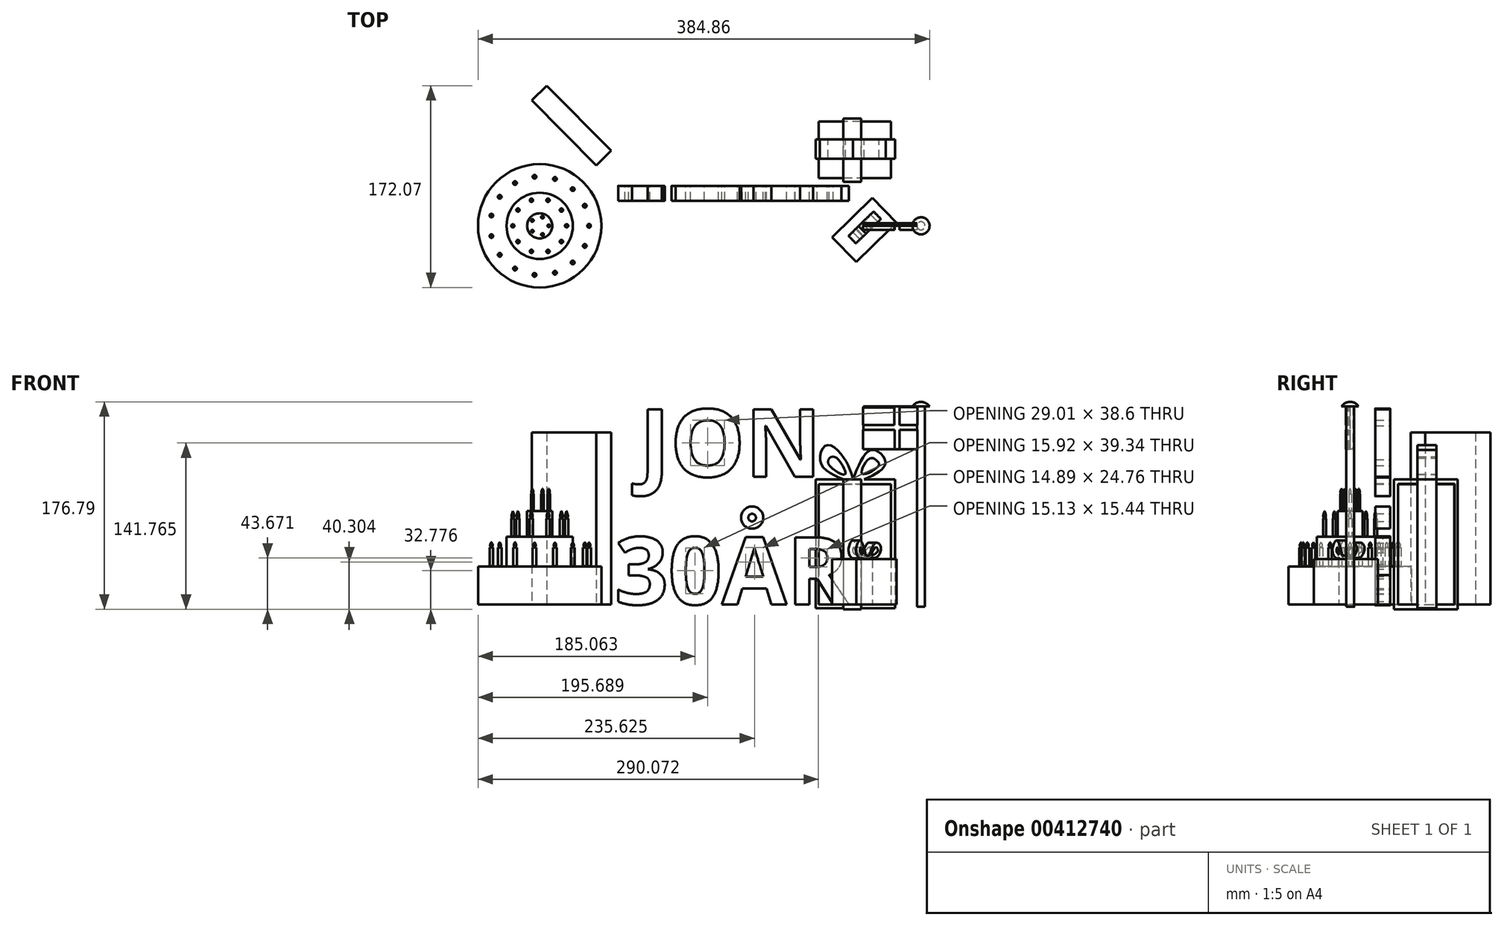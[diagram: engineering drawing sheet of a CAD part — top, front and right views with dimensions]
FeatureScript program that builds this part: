
annotation { "Feature Type Name" : "Feature", "Feature Type Description" : "" }
export const myFeature = defineFeature(function(context is Context, id is Id, definition is map)
    precondition{}
    {
        {
            var Q0;
            Q0=qCreatedBy(makeId("Front.planeOp"),FACE);
            var sketch = newSketch(context, id + "F0", { "sketchPlane" : qUnion([Q0])});
            skText(sketch, "E0", { "text": " JON\n30AR", "fontName": "OpenSans-Bold.ttf"});
            skCircle(sketch, "E1", {"center": v(45.9, -32.52) * mm, "radius": 9.45 * mm});
            skCircle(sketch, "E2", {"center": v(45.9, -32.52) * mm, "radius": 3.24 * mm});
            const initialGuessF0  = {"E0": [-0.07126, 0.00244, 1, 0, 0.05767]};
            skSetInitialGuess(sketch, initialGuessF0);
            skSolve(sketch);
        }
        {
            var Q0;
            Q0 = qSketchRegion(id + "F0", true);
            extrude(context, id + "F1", {"entities" : qUnion([Q0]), "depth" : 12.7 * mm});
        }
        {
            var Q0;
            Q0=qCreatedBy(makeId("Front.planeOp"),FACE);
            cPlane(context, id + "F2", {"entities" : qUnion([Q0]), "cplaneType" : CPlaneType.OFFSET, "offset" : 34.04 * mm, "width" : 152.4 * mm, "height" : 152.4 * mm});
        }
        {
            var Q0;
            Q0=makeQuery(id+"F1.opExtrude","SWEPT_FACE",FACE,{"disambiguationData":[OSD([sQuery(id+"F0.wireOp",EDGE,"E0.sketch_text.stroke-101")])]});
            var sketch = newSketch(context, id + "F3", { "sketchPlane" : qUnion([Q0])});
            skLineSegment(sketch, "E3", {"start": v(148.36, 10.23) * mm, "end": v(114.05, 43.78) * mm});
            skLineSegment(sketch, "E4", {"start": v(114.05, 43.78) * mm, "end": v(134.64, 64.84) * mm});
            skLineSegment(sketch, "E5", {"start": v(134.64, 64.84) * mm, "end": v(168.96, 31.3) * mm});
            skLineSegment(sketch, "E6", {"start": v(148.36, 10.23) * mm, "end": v(168.96, 31.3) * mm});
            skSolve(sketch);
        }
        {
            var Q0;
            Q0 = qSketchRegion(id + "F3", true);
            extrude(context, id + "F4", {"entities" : qUnion([Q0]), "oppositeDirection" : true, "depth" : 38.6 * mm});
        }
        {
            var Q0;
            Q0=makeQuery(id+"F4.opExtrude","SWEPT_FACE",FACE,{"disambiguationData":[OSD([sQuery(id+"F3.wireOp",EDGE,"E5")])]});
            cPlane(context, id + "F5", {"entities" : qUnion([Q0]), "cplaneType" : CPlaneType.OFFSET, "offset" : 16 * mm, "oppositeDirection" : true, "width" : 152.4 * mm, "height" : 152.4 * mm});
        }
        {
            var Q0;
            Q0=qCreatedBy(id+"F5.planeOp",FACE);
            var sketch = newSketch(context, id + "F6", { "sketchPlane" : qUnion([Q0])});
            skLineSegment(sketch, "E7", {"start": v(79.86, -67.82) * mm, "end": v(79.86, -66.38) * mm});
            skLineSegment(sketch, "E8", {"start": v(77.86, -64.93) * mm, "end": v(73.66, -64.93) * mm});
            skLineSegment(sketch, "E9", {"start": v(70.9, -67.21) * mm, "end": v(70.9, -68.06) * mm});
            skLineSegment(sketch, "E10", {"start": v(70.9, -68.06) * mm, "end": v(79.86, -67.82) * mm});
            skFitSpline(sketch, "E11", {"points": [v(77.86, -64.93) * mm, v(85.68, -53.9) * mm, v(91.43, -57.45) * mm, v(87.3, -66.01) * mm, v(79.86, -66.38) * mm], "startDerivative": vector(22.46, 50.64) * mm, "endDerivative": vector(-34.08, 6.92) * mm});
            skFitSpline(sketch, "E12", {"points": [v(80.8, -64.15) * mm, v(85.47, -57.91) * mm, v(87.84, -59.57) * mm, v(86.68, -62.36) * mm, v(80.8, -64.15) * mm]});
            skFitSpline(sketch, "E13", {"points": [v(73.66, -64.93) * mm, v(66.7, -52) * mm, v(61.8, -59.78) * mm, v(65.46, -66.74) * mm, v(70.9, -67.21) * mm], "startDerivative": vector(-19.87, 61.15) * mm, "endDerivative": vector(28.8, 3.24) * mm});
            skFitSpline(sketch, "E14", {"points": [v(70, -63.21) * mm, v(67.74, -58.1) * mm, v(67.06, -62.13) * mm, v(70, -63.21) * mm]});
            skPoint(sketch, "E15.orphan", {"position": v(79.86, -64.93) * mm});
            skSolve(sketch);
        }
        {
            var Q0;
            Q0 = qSketchRegion(id + "F6", true);
            extrude(context, id + "F7", {"entities" : qUnion([Q0]), "operationType" : NewBodyOperationType.ADD, "endBound" : BoundingType.SYMMETRIC, "depth" : 8.97 * mm});
        }
        {
            var Q0;
            Q0=makeQuery(id+"F1.opExtrude","SWEPT_FACE",FACE,{"disambiguationData":[OSD([sQuery(id+"F0.wireOp",EDGE,"E0.sketch_text.stroke-101")])]});
            var sketch = newSketch(context, id + "F8", { "sketchPlane" : qUnion([Q0])});
            skLineSegment(sketch, "E16.bottom", {"start": v(164.28, -6.74) * mm, "end": v(102.72, -6.74) * mm});
            skLineSegment(sketch, "E16.top", {"start": v(164.28, -54.83) * mm, "end": v(102.72, -54.83) * mm});
            skLineSegment(sketch, "E16.left", {"start": v(164.28, -6.74) * mm, "end": v(164.28, -54.83) * mm});
            skLineSegment(sketch, "E16.right", {"start": v(102.72, -6.74) * mm, "end": v(102.72, -54.83) * mm});
            skSolve(sketch);
        }
        {
            var Q0;
            Q0=makeQuery(id+"F8.imprint","IMPRINT",FACE,{"disambiguationData":[TD([[makeQuery(id+"F8.imprint","IMPRINT",EDGE,{"derivedFrom":sQuery(id+"F8.wireOp",EDGE,"E16.bottom")}),1.0]])]});
            extrude(context, id + "F9", {"entities" : qUnion([Q0]), "oppositeDirection" : true, "depth" : 102.36 * mm});
        }
        {
            var Q0;
            Q0=makeQuery(id+"F9.opExtrude","SWEPT_FACE",FACE,{"disambiguationData":[OSD([sQuery(id+"F8.wireOp",EDGE,"E16.left")])]});
            cPlane(context, id + "F10", {"entities" : qUnion([Q0]), "cplaneType" : CPlaneType.OFFSET, "offset" : 33.02 * mm, "oppositeDirection" : true, "width" : 152.4 * mm, "height" : 152.4 * mm});
        }
        {
            var Q0;
            Q0=qCreatedBy(id+"F10.planeOp",FACE);
            var sketch = newSketch(context, id + "F11", { "sketchPlane" : qUnion([Q0])});
            skLineSegment(sketch, "E17.bottom", {"start": v(6.87, -3.88) * mm, "end": v(54.94, -3.88) * mm});
            skLineSegment(sketch, "E17.top", {"start": v(6.87, -106.27) * mm, "end": v(54.94, -106.27) * mm});
            skLineSegment(sketch, "E17.left", {"start": v(6.87, -3.88) * mm, "end": v(6.87, -106.27) * mm});
            skLineSegment(sketch, "E17.right", {"start": v(54.94, -3.88) * mm, "end": v(54.94, -106.27) * mm});
            skLineSegment(sketch, "E18.bottom", {"start": v(3.43, 0) * mm, "end": v(57.44, 0) * mm});
            skLineSegment(sketch, "E18.top", {"start": v(3.43, -110.64) * mm, "end": v(57.44, -110.64) * mm});
            skLineSegment(sketch, "E18.left", {"start": v(3.43, 0) * mm, "end": v(3.43, -110.64) * mm});
            skLineSegment(sketch, "E18.right", {"start": v(57.44, 0) * mm, "end": v(57.44, -110.64) * mm});
            skSolve(sketch);
        }
        {
            var Q0;
            Q0 = qSketchRegion(id + "F11", true);
            extrude(context, id + "F12", {"entities" : qUnion([Q0]), "operationType" : NewBodyOperationType.ADD, "endBound" : BoundingType.SYMMETRIC, "depth" : 15.24 * mm});
        }
        {
            var Q0;
            {var subQ0=sQuery(id+"F8.wireOp",EDGE,"E16.right");var subQ3=sQuery(id+"F8.wireOp",EDGE,"E16.bottom");Q0=makeQuery(id+"F12.boolean.opBoolean","SPLIT",FACE,{"disambiguationData":[TD([makeQuery(id+"F9.opExtrude","SWEPT_FACE",FACE,{"disambiguationData":[OSD([subQ0])]})])],"derivedFrom":makeQuery(id+"F9.opExtrude","SWEPT_FACE",FACE,{"disambiguationData":[OSD([subQ3])]})});}
            cPlane(context, id + "F13", {"entities" : qUnion([Q0]), "cplaneType" : CPlaneType.OFFSET, "offset" : 24.64 * mm, "oppositeDirection" : true, "width" : 152.4 * mm, "height" : 152.4 * mm});
        }
        {
            var Q0;
            Q0=qCreatedBy(id+"F13.planeOp",FACE);
            var sketch = newSketch(context, id + "F14", { "sketchPlane" : qUnion([Q0])});
            skLineSegment(sketch, "E19.bottom", {"start": v(100.07, 0) * mm, "end": v(123.93, 0) * mm});
            skLineSegment(sketch, "E19.top", {"start": v(100.07, -109.7) * mm, "end": v(167.8, -109.7) * mm});
            skLineSegment(sketch, "E19.left", {"start": v(100.07, 0) * mm, "end": v(100.07, -109.7) * mm});
            skLineSegment(sketch, "E19.right", {"start": v(167.8, 0) * mm, "end": v(167.8, -109.7) * mm});
            skFitSpline(sketch, "E20", {"points": [v(141.31, 0) * mm, v(159.6, 14.61) * mm, v(148.23, 25.19) * mm, v(131.96, 0) * mm], "startDerivative": vector(81.32, 38.17) * mm, "endDerivative": vector(-36.19, -96.91) * mm});
            skFitSpline(sketch, "E21", {"points": [v(131.96, 0) * mm, v(124.85, 17.26) * mm, v(109.4, 29.25) * mm, v(104.22, 14.51) * mm, v(123.93, 0) * mm], "startDerivative": vector(-19.08, 67.84) * mm, "endDerivative": vector(94.35, -39.58) * mm});
            skFitSpline(sketch, "E22", {"points": [v(139.69, 4.96) * mm, v(146.1, 17.87) * mm, v(152.3, 15.73) * mm, v(153.71, 11.77) * mm, v(139.69, 4.96) * mm]});
            skFitSpline(sketch, "E23", {"points": [v(124.65, 4.15) * mm, v(123.93, 10.14) * mm, v(114.89, 19.5) * mm, v(110.72, 14) * mm, v(124.65, 4.15) * mm]});
            skLineSegment(sketch, "E24.trimOffspring", {"start": v(141.31, 0) * mm, "end": v(167.8, 0) * mm});
            skSolve(sketch);
        }
        {
            var Q0;
            Q0 = qSketchRegion(id + "F14", true);
            extrude(context, id + "F15", {"entities" : qUnion([Q0]), "operationType" : NewBodyOperationType.ADD, "endBound" : BoundingType.SYMMETRIC, "depth" : 16.26 * mm});
        }
        {
            var Q0;
            Q0=qCreatedBy(id+"F2.planeOp",FACE);
            var sketch = newSketch(context, id + "F16", { "sketchPlane" : qUnion([Q0])});
            skLineSegment(sketch, "E25.top", {"start": v(189.8, -108.55) * mm, "end": v(193.24, -108.55) * mm});
            skLineSegment(sketch, "E25.left", {"start": v(189.8, 62.15) * mm, "end": v(189.8, -108.55) * mm});
            skLineSegment(sketch, "E25.right", {"start": v(193.24, 62.15) * mm, "end": v(193.24, -108.55) * mm});
            skArc(sketch, "E26", {"start": v(197.12, 62.15) * mm, "mid": v(193.97, 65.08) * mm, "end": v(189.8, 66.15) * mm});
            skLineSegment(sketch, "E27", {"start": v(189.8, 62.15) * mm, "end": v(189.8, 66.15) * mm});
            skLineSegment(sketch, "E28", {"start": v(193.24, 62.15) * mm, "end": v(197.12, 62.15) * mm});
            skSolve(sketch);
        }
        {
            var Q0;
            Q0 = qSketchRegion(id + "F16", true);
            var Q1;
            Q1=sQuery(id+"F16.wireOp",EDGE,"E25.left");
            revolve(context, id + "F17", {"entities" : qUnion([Q0]), "axis" : qUnion([Q1]), "revolveType" : RevolveType.FULL});
        }
        {
            var Q0;
            Q0=qCreatedBy(id+"F2.planeOp",FACE);
            var sketch = newSketch(context, id + "F18", { "sketchPlane" : qUnion([Q0])});
            skLineSegment(sketch, "E29.bottom", {"start": v(186.75, 61.65) * mm, "end": v(171.4, 61.65) * mm});
            skLineSegment(sketch, "E29.top", {"start": v(186.75, 46.3) * mm, "end": v(171.4, 46.3) * mm});
            skLineSegment(sketch, "E29.left", {"start": v(186.75, 61.65) * mm, "end": v(186.75, 46.3) * mm});
            skLineSegment(sketch, "E29.right", {"start": v(171.4, 61.65) * mm, "end": v(171.4, 46.3) * mm});
            skLineSegment(sketch, "E30.bottom", {"start": v(186.75, 42.21) * mm, "end": v(171.4, 42.21) * mm});
            skLineSegment(sketch, "E30.top", {"start": v(186.75, 25.88) * mm, "end": v(171.4, 25.88) * mm});
            skLineSegment(sketch, "E30.left", {"start": v(186.75, 42.21) * mm, "end": v(186.75, 25.88) * mm});
            skLineSegment(sketch, "E30.right", {"start": v(171.4, 42.21) * mm, "end": v(171.4, 25.88) * mm});
            skLineSegment(sketch, "E31.bottom", {"start": v(167.12, 61.46) * mm, "end": v(140.3, 61.46) * mm});
            skLineSegment(sketch, "E31.top", {"start": v(167.12, 46.3) * mm, "end": v(140.3, 46.3) * mm});
            skLineSegment(sketch, "E31.left", {"start": v(167.12, 61.46) * mm, "end": v(167.12, 46.3) * mm});
            skLineSegment(sketch, "E31.right", {"start": v(140.3, 61.46) * mm, "end": v(140.3, 46.3) * mm});
            skLineSegment(sketch, "E32.bottom", {"start": v(167.5, 42.21) * mm, "end": v(140.3, 42.21) * mm});
            skLineSegment(sketch, "E32.top", {"start": v(167.5, 25.7) * mm, "end": v(140.3, 25.7) * mm});
            skLineSegment(sketch, "E32.left", {"start": v(167.5, 42.21) * mm, "end": v(167.5, 25.7) * mm});
            skLineSegment(sketch, "E32.right", {"start": v(140.3, 42.21) * mm, "end": v(140.3, 25.7) * mm});
            skSolve(sketch);
        }
        {
            var Q0;
            Q0 = qSketchRegion(id + "F18", true);
            extrude(context, id + "F19", {"entities" : qUnion([Q0]), "operationType" : NewBodyOperationType.ADD, "depth" : 3.56 * mm});
        }
        {
            var Q0;
            Q0=makeQuery(id+"F19.opExtrude","CAP_FACE",FACE,{"disambiguationData":[OSD([sQuery(id+"F18.wireOp",EDGE,"E30.bottom"),sQuery(id+"F18.wireOp",EDGE,"E30.top"),sQuery(id+"F18.wireOp",EDGE,"E30.left"),sQuery(id+"F18.wireOp",EDGE,"E30.right")])],"isStart":true});
            var sketch = newSketch(context, id + "F20", { "sketchPlane" : qUnion([Q0])});
            skLineSegment(sketch, "E33.bottom", {"start": v(-140.68, 62.3) * mm, "end": v(-186.37, 62.3) * mm});
            skLineSegment(sketch, "E33.top", {"start": v(-140.68, 25.88) * mm, "end": v(-186.37, 25.88) * mm});
            skLineSegment(sketch, "E33.left", {"start": v(-140.68, 62.3) * mm, "end": v(-140.68, 25.88) * mm});
            skLineSegment(sketch, "E33.right", {"start": v(-186.37, 62.3) * mm, "end": v(-186.37, 25.88) * mm});
            skSolve(sketch);
        }
        {
            var Q0;
            Q0 = qSketchRegion(id + "F20", true);
            extrude(context, id + "F21", {"entities" : qUnion([Q0]), "depth" : 2.3 * mm});
        }
        {
            var Q0;
            Q0=qCreatedBy(id+"F2.planeOp",FACE);
            var sketch = newSketch(context, id + "F22", { "sketchPlane" : qUnion([Q0])});
            skLineSegment(sketch, "E34", {"start": v(-82.55, -106.72) * mm, "end": v(-82.55, -74.09) * mm});
            skLineSegment(sketch, "E35", {"start": v(-82.55, -74.09) * mm, "end": v(-106.9, -74.09) * mm});
            skLineSegment(sketch, "E36", {"start": v(-106.9, -74.09) * mm, "end": v(-106.9, -48.76) * mm});
            skLineSegment(sketch, "E37", {"start": v(-106.9, -48.76) * mm, "end": v(-124.43, -48.76) * mm});
            skLineSegment(sketch, "E38", {"start": v(-124.43, -48.76) * mm, "end": v(-124.43, -26.85) * mm});
            skLineSegment(sketch, "E39", {"start": v(-124.43, -26.85) * mm, "end": v(-135.14, -26.85) * mm});
            skLineSegment(sketch, "E40", {"start": v(-135.14, -26.85) * mm, "end": v(-135.14, -106.72) * mm});
            skLineSegment(sketch, "E41", {"start": v(-82.55, -106.72) * mm, "end": v(-135.14, -106.72) * mm});
            skSolve(sketch);
        }
        {
            var Q0;
            Q0 = qSketchRegion(id + "F22", true);
            var Q1;
            Q1=sQuery(id+"F22.wireOp",EDGE,"E40");
            revolve(context, id + "F23", {"entities" : qUnion([Q0]), "axis" : qUnion([Q1]), "revolveType" : RevolveType.FULL});
        }
        {
            var Q0;
            Q0=qCreatedBy(id+"F2.planeOp",FACE);
            var sketch = newSketch(context, id + "F24", { "sketchPlane" : qUnion([Q0])});
            skLineSegment(sketch, "E42.bottom", {"start": v(-91.52, -73.86) * mm, "end": v(-93.08, -73.86) * mm});
            skLineSegment(sketch, "E42.top", {"start": v(-91.52, -58.06) * mm, "end": v(-92.5, -58.06) * mm});
            skLineSegment(sketch, "E42.left", {"start": v(-91.52, -73.86) * mm, "end": v(-91.52, -58.06) * mm});
            skLineSegment(sketch, "E42.right", {"start": v(-93.08, -73.86) * mm, "end": v(-93.08, -58.06) * mm});
            skLineSegment(sketch, "E43", {"start": v(-93.08, -58.06) * mm, "end": v(-93.08, -53.56) * mm});
            skFitSpline(sketch, "E44", {"points": [v(-93.08, -53.56) * mm, v(-92.02, -55.67) * mm, v(-92.5, -58.06) * mm], "startDerivative": vector(2.9, -4.14) * mm, "endDerivative": vector(-1.76, -4.86) * mm});
            skSolve(sketch);
        }
        {
            var Q0;
            Q0 = qSketchRegion(id + "F24", true);
            var Q1;
            Q1=sQuery(id+"F24.wireOp",EDGE,"E42.right");
            revolve(context, id + "F25", {"entities" : qUnion([Q0]), "axis" : qUnion([Q1]), "revolveType" : RevolveType.FULL});
        }
        {
            var Q0;
            Q0=makeQuery(id+"F25.opRevolve","SWEPT_BODY",BODY,{"disambiguationData":[OSD([sQuery(id+"F24.wireOp",EDGE,"E42.bottom"),sQuery(id+"F24.wireOp",EDGE,"E42.top"),sQuery(id+"F24.wireOp",EDGE,"E42.left"),sQuery(id+"F24.wireOp",EDGE,"E42.right"),sQuery(id+"F24.wireOp",EDGE,"E43"),sQuery(id+"F24.wireOp",EDGE,"E44")])]});
            var Q1;
            Q1=makeQuery(id+"F23.opRevolve","SWEPT_FACE",FACE,{"disambiguationData":[OSD([sQuery(id+"F22.wireOp",EDGE,"E38")])]});
            circularPattern(context, id + "F26", {"entities" : qUnion([Q0]), "axis" : qUnion([Q1]), "angle" : 360 * degree, "instanceCount" : 15, "equalSpace" : true});
        }
        {
            var Q0;
            Q0=qCreatedBy(id+"F2.planeOp",FACE);
            var sketch = newSketch(context, id + "F27", { "sketchPlane" : qUnion([Q0])});
            skLineSegment(sketch, "E45.bottom", {"start": v(-110.86, -48.55) * mm, "end": v(-112.24, -48.55) * mm});
            skLineSegment(sketch, "E45.top", {"start": v(-110.86, -33.34) * mm, "end": v(-111.55, -33.34) * mm});
            skLineSegment(sketch, "E45.left", {"start": v(-110.86, -48.55) * mm, "end": v(-110.86, -33.34) * mm});
            skLineSegment(sketch, "E45.right", {"start": v(-112.24, -48.55) * mm, "end": v(-112.24, -33.34) * mm});
            skLineSegment(sketch, "E46", {"start": v(-112.24, -33.34) * mm, "end": v(-112.24, -26.9) * mm});
            skFitSpline(sketch, "E47", {"points": [v(-112.24, -26.9) * mm, v(-111.14, -30.68) * mm, v(-111.55, -33.34) * mm], "startDerivative": vector(2.82, -7.18) * mm, "endDerivative": vector(-1.57, -5.65) * mm});
            skSolve(sketch);
        }
        {
            var Q0;
            Q0 = qSketchRegion(id + "F27", true);
            var Q1;
            Q1=sQuery(id+"F27.wireOp",EDGE,"E46");
            revolve(context, id + "F28", {"entities" : qUnion([Q0]), "axis" : qUnion([Q1]), "revolveType" : RevolveType.FULL});
        }
        {
            var Q0;
            Q0=makeQuery(id+"F28.opRevolve","SWEPT_BODY",BODY,{"disambiguationData":[OSD([sQuery(id+"F27.wireOp",EDGE,"E45.bottom"),sQuery(id+"F27.wireOp",EDGE,"E45.top"),sQuery(id+"F27.wireOp",EDGE,"E45.left"),sQuery(id+"F27.wireOp",EDGE,"E45.right"),sQuery(id+"F27.wireOp",EDGE,"E46"),sQuery(id+"F27.wireOp",EDGE,"E47")])]});
            var Q1;
            Q1=makeQuery(id+"F23.opRevolve","SWEPT_FACE",FACE,{"disambiguationData":[OSD([sQuery(id+"F22.wireOp",EDGE,"E38")])]});
            circularPattern(context, id + "F29", {"entities" : qUnion([Q0]), "axis" : qUnion([Q1]), "angle" : 360 * degree, "instanceCount" : 10, "equalSpace" : true});
        }
        {
            var Q0;
            Q0=qCreatedBy(id+"F2.planeOp",FACE);
            var sketch = newSketch(context, id + "F30", { "sketchPlane" : qUnion([Q0])});
            skLineSegment(sketch, "E48.bottom", {"start": v(-126.26, -26.7) * mm, "end": v(-127.38, -26.7) * mm});
            skLineSegment(sketch, "E48.top", {"start": v(-126.26, -12.42) * mm, "end": v(-126.82, -12.42) * mm});
            skLineSegment(sketch, "E48.left", {"start": v(-126.26, -26.7) * mm, "end": v(-126.26, -12.42) * mm});
            skLineSegment(sketch, "E48.right", {"start": v(-127.38, -26.7) * mm, "end": v(-127.38, -12.42) * mm});
            skLineSegment(sketch, "E49", {"start": v(-127.38, -12.42) * mm, "end": v(-127.38, -7.72) * mm});
            skFitSpline(sketch, "E50", {"points": [v(-127.38, -7.72) * mm, v(-126.49, -10.32) * mm, v(-126.82, -12.42) * mm], "startDerivative": vector(2.3, -4.99) * mm, "endDerivative": vector(-1.26, -4.4) * mm});
            skSolve(sketch);
        }
        {
            var Q0;
            Q0 = qSketchRegion(id + "F30", true);
            var Q1;
            Q1=sQuery(id+"F30.wireOp",EDGE,"E48.right");
            revolve(context, id + "F31", {"entities" : qUnion([Q0]), "axis" : qUnion([Q1]), "revolveType" : RevolveType.FULL});
        }
        {
            var Q0;
            Q0=makeQuery(id+"F31.opRevolve","SWEPT_BODY",BODY,{"disambiguationData":[OSD([sQuery(id+"F30.wireOp",EDGE,"E48.bottom"),sQuery(id+"F30.wireOp",EDGE,"E48.top"),sQuery(id+"F30.wireOp",EDGE,"E48.left"),sQuery(id+"F30.wireOp",EDGE,"E48.right"),sQuery(id+"F30.wireOp",EDGE,"E49"),sQuery(id+"F30.wireOp",EDGE,"E50")])]});
            var Q1;
            Q1=makeQuery(id+"F23.opRevolve","SWEPT_FACE",FACE,{"disambiguationData":[OSD([sQuery(id+"F22.wireOp",EDGE,"E38")])]});
            circularPattern(context, id + "F32", {"entities" : qUnion([Q0]), "axis" : qUnion([Q1]), "angle" : 360 * degree, "instanceCount" : 5, "equalSpace" : true});
        }
        {
            var Q0;
            Q0=makeQuery(id+"F1.opExtrude","SWEPT_FACE",FACE,{"disambiguationData":[OSD([sQuery(id+"F0.wireOp",EDGE,"E0.sketch_text.stroke-84")])]});
            var sketch = newSketch(context, id + "F33", { "sketchPlane" : qUnion([Q0])});
            skLineSegment(sketch, "E51", {"start": v(-86.95, -17.5) * mm, "end": v(-74.28, -30.06) * mm});
            skLineSegment(sketch, "E52", {"start": v(-74.28, -30.06) * mm, "end": v(-129.16, -85.44) * mm});
            skLineSegment(sketch, "E53", {"start": v(-86.95, -17.5) * mm, "end": v(-141.83, -72.88) * mm});
            skLineSegment(sketch, "E54", {"start": v(-141.83, -72.88) * mm, "end": v(-129.16, -85.44) * mm});
            skPoint(sketch, "E55.orphan", {"position": v(-196.71, -128.26) * mm});
            skPoint(sketch, "E56.orphan", {"position": v(-184.04, -140.81) * mm});
            skSolve(sketch);
        }
        {
            var Q0;
            Q0 = qSketchRegion(id + "F33", true);
            extrude(context, id + "F34", {"entities" : qUnion([Q0]), "oppositeDirection" : true, "depth" : 146.56 * mm});
        }
    });
